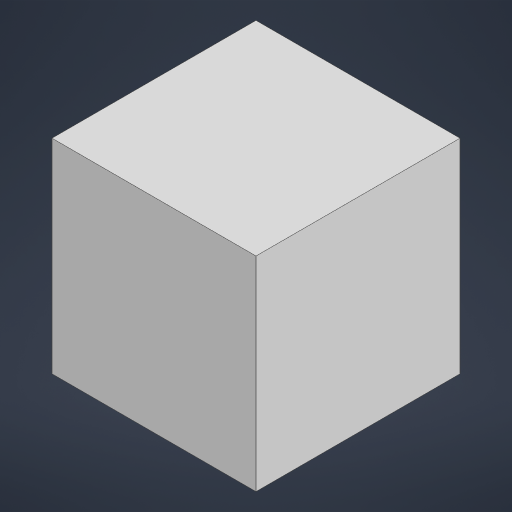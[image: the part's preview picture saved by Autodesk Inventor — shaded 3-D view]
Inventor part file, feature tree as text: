
AUTODESK INVENTOR PART (.ipt)
format: ipt  version: 2024.2 (Build 282272000, 272)  size: 164,864 bytes
history: native  units: mm
features: extrude x1, sketch x1
ambient origin geometry x8: Origin, YZ Plane, XZ Plane, XY Plane, X Axis, Y Axis, Z Axis, Center Point
bodies: Solid1 (feature_tree)
feature tree (2):
  extrude  "Extrusion1"  Depth=15.0mm
  sketch  "Sketch1"  dims[d0=15.0mm d1=15.0mm d2=15.0mm d3=0.0mm]
